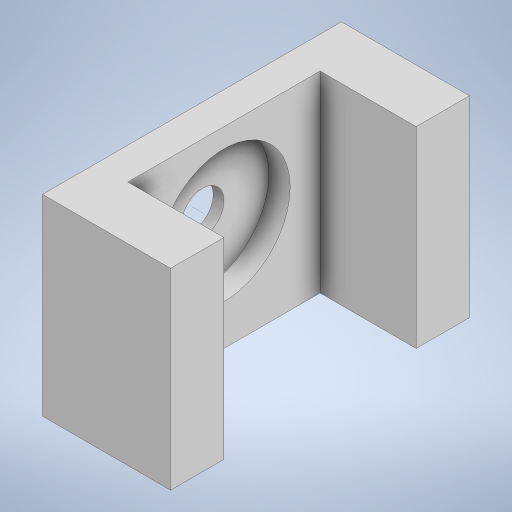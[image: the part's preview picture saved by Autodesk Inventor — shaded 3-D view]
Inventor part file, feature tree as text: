
AUTODESK INVENTOR PART (.ipt)
format: ipt  version: 2023 (Build 270158000, 158)  size: 258,048 bytes
history: native  units: mm
features: extrude x8, sketch x8
ambient origin geometry x8: Origin, YZ Plane, XZ Plane, XY Plane, X Axis, Y Axis, Z Axis, Center Point
bodies: Solid1 (feature_tree)
feature tree (16):
  extrude  "Extrusion1"  Depth=18.0mm
  extrude  "Extrusion2"  Depth=1.0mm
  extrude  "Extrusion3"  Depth=5.0mm TaperAngle=0.0deg
  extrude  "Extrusion4"  Depth=5.0mm TaperAngle=0.0deg
  extrude  "Extrusion5"  Depth=4.0mm TaperAngle=0.0deg
  extrude  "Extrusion6"  Depth=12.0mm
  extrude  "Extrusion7"  Depth=2.0mm
  extrude  "Extrusion8"  [1 undecoded]
  sketch  "Sketch1"  dims[d0=18.0mm d1=20.0mm]
  sketch  "Sketch2"  dims[d2=3.0mm d3=0.0mm d4=1.0mm]
  sketch  "Sketch3"  dims[d5=1.0mm d6=5.0mm d7=0.0mm]
  sketch  "Sketch4"  dims[d8=4.0mm d9=5.0mm d10=0.0mm]
  sketch  "Sketch5"  dims[d11=4.0mm d12=0.0mm d13=4.0mm d14=0.0mm]
  sketch  "Sketch6"  dims[d15=4.0mm d16=0.0mm d17=12.0mm]
  sketch  "Sketch7"  dims[d18=2.0mm d19=0.0mm d20=12.4mm]
  sketch  "Sketch8"  dims[d21=2.0mm d22=0.0mm]
note: 1 required parameter value undecoded (feature->parameter linkage not recoverable at this tier; creation-order binding heuristic only, values carry confidence <= 0.55)
